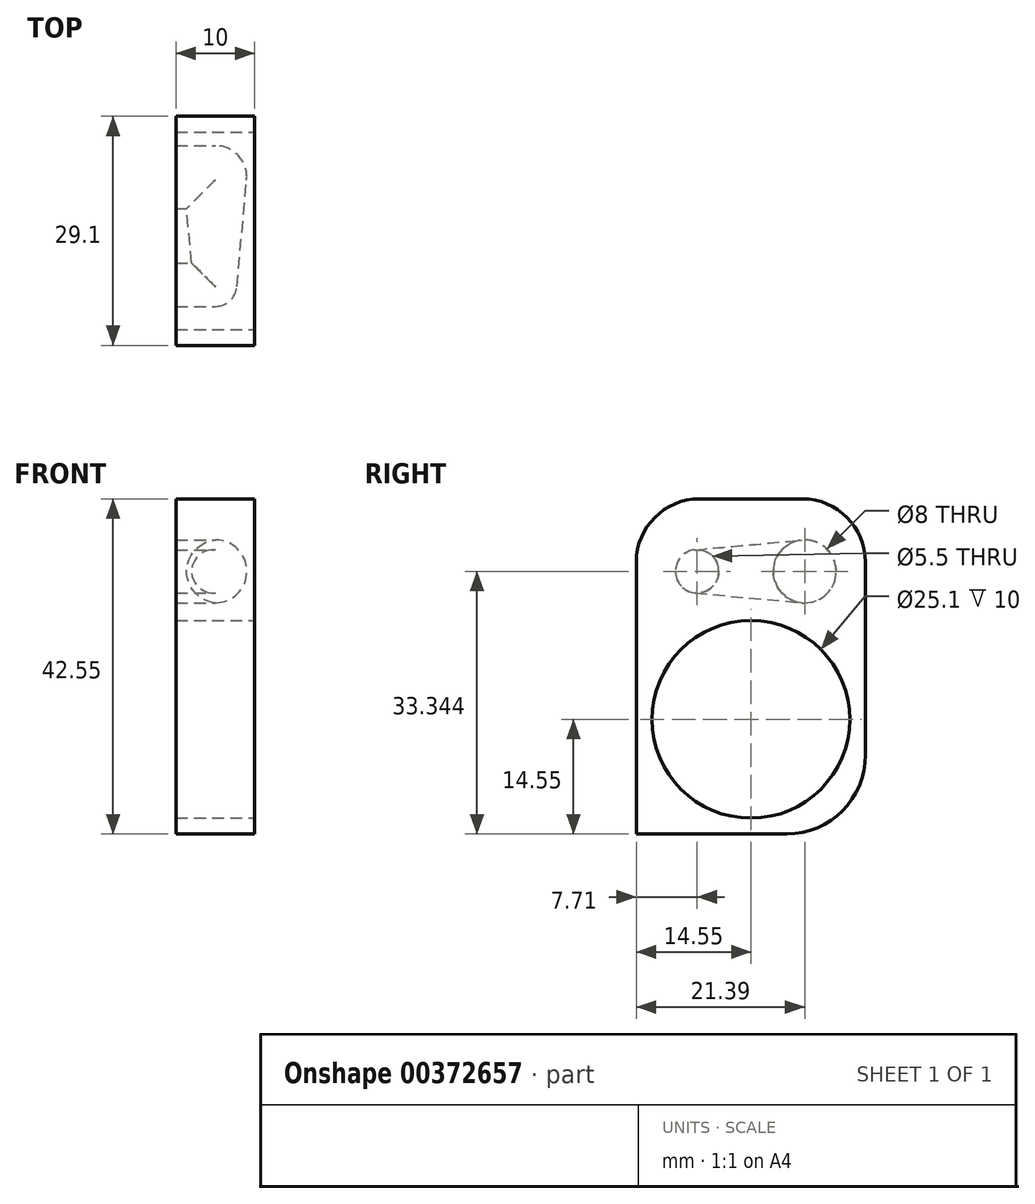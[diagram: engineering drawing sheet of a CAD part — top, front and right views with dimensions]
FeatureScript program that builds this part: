
annotation { "Feature Type Name" : "Feature", "Feature Type Description" : "" }
export const myFeature = defineFeature(function(context is Context, id is Id, definition is map)
    precondition{}
    {
        {
            var Q0;
            Q0=qCreatedBy(makeId("Right.planeOp"),FACE);
            var sketch = newSketch(context, id + "F0", { "sketchPlane" : qUnion([Q0])});
            skCircle(sketch, "E0", {"center": v(0, 0) * mm, "radius": 12.55 * mm});
            skCircle(sketch, "E1", {"center": v(-6.84, 18.8) * mm, "radius": 4.3 * mm, "construction": true});
            skCircle(sketch, "E2", {"center": v(6.84, 18.8) * mm, "radius": 5.1 * mm, "construction": true});
            skLineSegment(sketch, "E3", {"start": v(-6.84, 18.8) * mm, "end": v(0, 0) * mm, "construction": true});
            skLineSegment(sketch, "E4", {"start": v(6.84, 18.8) * mm, "end": v(0, 0) * mm, "construction": true});
            skCircle(sketch, "E5", {"center": v(-27, 0) * mm, "radius": 11 * mm});
            skLineSegment(sketch, "E6", {"start": v(-27, 0) * mm, "end": v(0, 0) * mm, "construction": true});
            skLineSegment(sketch, "E7", {"start": v(6.55, 28) * mm, "end": v(-6.55, 28) * mm});
            skLineSegment(sketch, "E8", {"start": v(14.55, 20) * mm, "end": v(14.55, -14.55) * mm});
            skLineSegment(sketch, "E9", {"start": v(-14.55, 20) * mm, "end": v(-14.55, -14.55) * mm});
            skLineSegment(sketch, "E10", {"start": v(-14.55, -14.55) * mm, "end": v(14.55, -14.55) * mm});
            skCircle(sketch, "E11", {"center": v(-6.84, 18.8) * mm, "radius": 2.75 * mm});
            skCircle(sketch, "E12", {"center": v(6.84, 18.8) * mm, "radius": 4 * mm});
            skLineSegment(sketch, "E13", {"start": v(-9.6, 18.8) * mm, "end": v(10.84, 18.8) * mm});
            skLineSegment(sketch, "E14", {"start": v(-7.1, 21.53) * mm, "end": v(6.84, 22.81) * mm});
            skLineSegment(sketch, "E15", {"start": v(0, 0) * mm, "end": v(0, -14.55) * mm, "construction": true});
            skPoint(sketch, "E16.visualSharp", {"position": v(-14.55, 28) * mm});
            skArc(sketch, "E16.filletArc", {"start": v(-6.55, 28) * mm, "mid": v(-12.2, 25.66) * mm, "end": v(-14.55, 20) * mm});
            skPoint(sketch, "E17.visualSharp", {"position": v(14.55, 28) * mm});
            skArc(sketch, "E17.filletArc", {"start": v(14.55, 20) * mm, "mid": v(12.2, 25.66) * mm, "end": v(6.55, 28) * mm});
            skSolve(sketch);
        }
        {
            var Q0;
            Q0=makeQuery(id+"F0.imprint","IMPRINT",FACE,{"disambiguationData":[TD([[makeQuery(id+"F0.imprint","IMPRINT",EDGE,{"derivedFrom":sQuery(id+"F0.wireOp",EDGE,"E0")}),-1.0]])]});
            var Q1;
            {var subQ0=sQuery(id+"F0.wireOp",EDGE,"E14");var subQ1=sQuery(id+"F0.wireOp",EDGE,"E11");var subQ2=makeQuery(id+"F0.imprint","INTERSECT",VERTEX,{"derivedFrom":[subQ1,subQ0]});Q1=makeQuery(id+"F0.imprint","IMPRINT",FACE,{"disambiguationData":[TD([[makeQuery(id+"F0.imprint","IMPRINT",EDGE,{"disambiguationData":[TD([[subQ2,1.0]])],"derivedFrom":subQ1}),-1.0]])]});}
            extrude(context, id + "F1", {"entities" : qUnion([Q0, Q1]), "oppositeDirection" : true, "depth" : 5 * mm, "offsetDistance" : 25 * mm});
        }
        {
            var Q0;
            Q0=makeQuery(id+"F0.imprint","IMPRINT",FACE,{"disambiguationData":[TD([[makeQuery(id+"F0.imprint","IMPRINT",EDGE,{"derivedFrom":sQuery(id+"F0.wireOp",EDGE,"E0")}),-1.0]])]});
            var Q1;
            {var subQ0=sQuery(id+"F0.wireOp",EDGE,"E13");var subQ1=sQuery(id+"F0.wireOp",EDGE,"E11");var subQ2=makeQuery(id+"F0.imprint","INTERSECT",VERTEX,{"disambiguationData":[OD(0.0)],"derivedFrom":[subQ1,subQ0]});Q1=makeQuery(id+"F0.imprint","IMPRINT",FACE,{"disambiguationData":[TD([[makeQuery(id+"F0.imprint","IMPRINT",EDGE,{"disambiguationData":[TD([[subQ2,-1.0]])],"derivedFrom":subQ1}),1.0]])]});}
            var Q2;
            {var subQ0=sQuery(id+"F0.wireOp",EDGE,"E11");var subQ1=makeQuery(id+"F0.imprint","INTERSECT",VERTEX,{"derivedFrom":[subQ0,sQuery(id+"F0.wireOp",EDGE,"E14")]});Q2=makeQuery(id+"F0.imprint","IMPRINT",FACE,{"disambiguationData":[TD([[makeQuery(id+"F0.imprint","IMPRINT",EDGE,{"disambiguationData":[TD([[subQ1,1.0]])],"derivedFrom":subQ0}),1.0]])]});}
            var Q3;
            {var subQ0=sQuery(id+"F0.wireOp",EDGE,"E14");var subQ1=sQuery(id+"F0.wireOp",EDGE,"E11");var subQ2=makeQuery(id+"F0.imprint","INTERSECT",VERTEX,{"derivedFrom":[subQ1,subQ0]});Q3=makeQuery(id+"F0.imprint","IMPRINT",FACE,{"disambiguationData":[TD([[makeQuery(id+"F0.imprint","IMPRINT",EDGE,{"disambiguationData":[TD([[subQ2,1.0]])],"derivedFrom":subQ1}),-1.0]])]});}
            var Q4;
            {var subQ0=sQuery(id+"F0.wireOp",EDGE,"E13");var subQ1=sQuery(id+"F0.wireOp",EDGE,"E12");var subQ2=makeQuery(id+"F0.imprint","INTERSECT",VERTEX,{"disambiguationData":[OD(0.0)],"derivedFrom":[subQ1,subQ0]});Q4=makeQuery(id+"F0.imprint","IMPRINT",FACE,{"disambiguationData":[TD([[makeQuery(id+"F0.imprint","IMPRINT",EDGE,{"disambiguationData":[TD([[subQ2,-1.0]])],"derivedFrom":subQ1}),1.0]])]});}
            var Q5;
            {var subQ0=sQuery(id+"F0.wireOp",EDGE,"E13");var subQ1=sQuery(id+"F0.wireOp",EDGE,"E12");var subQ2=makeQuery(id+"F0.imprint","INTERSECT",VERTEX,{"disambiguationData":[OD(0.0)],"derivedFrom":[subQ1,subQ0]});Q5=makeQuery(id+"F0.imprint","IMPRINT",FACE,{"disambiguationData":[TD([[makeQuery(id+"F0.imprint","IMPRINT",EDGE,{"disambiguationData":[TD([[subQ2,1.0]])],"derivedFrom":subQ1}),1.0]])]});}
            extrude(context, id + "F2", {"entities" : qUnion([Q0, Q1, Q2, Q3, Q4, Q5]), "operationType" : NewBodyOperationType.ADD, "depth" : 5 * mm, "offsetDistance" : 25 * mm});
        }
        {
            var Q0;
            Q0=makeQuery(id+"F1.opExtrude","SWEPT_EDGE",EDGE,{"disambiguationData":[OSD([sQuery(id+"F0.wireOp",EDGE,"XYx4FfuK-tnTQ-wQDn-o0lU-hYzAaBfXhwYU"),sQuery(id+"F0.wireOp",EDGE,"E7")])]});
            var Q1;
            Q1=makeQuery(id+"F1.opExtrude","SWEPT_EDGE",EDGE,{"disambiguationData":[OSD([sQuery(id+"F0.wireOp",EDGE,"ezvYwHDF-qibp-4aTS-obrj-ytzPbMtdMMT9"),sQuery(id+"F0.wireOp",EDGE,"E8")])]});
            var Q2;
            Q2=makeQuery(id+"F1.opExtrude","SWEPT_EDGE",EDGE,{"disambiguationData":[OSD([sQuery(id+"F0.wireOp",EDGE,"ezvYwHDF-qibp-4aTS-obrj-ytzPbMtdMMT9"),sQuery(id+"F0.wireOp",EDGE,"E7")])]});
            var Q3;
            Q3=makeQuery(id+"F1.opExtrude","SWEPT_EDGE",EDGE,{"disambiguationData":[OSD([sQuery(id+"F0.wireOp",EDGE,"E8"),sQuery(id+"F0.wireOp",EDGE,"E10")])]});
            fillet(context, id + "F3", {"entities" : qUnion([Q0, Q1, Q2, Q3]), "radius" : 10 * mm, "tangentPropagation" : true, "allowEdgeOverflow" : false});
        }
        {
            var Q0;
            {var subQ0=sQuery(id+"F0.wireOp",EDGE,"E11");var subQ1=makeQuery(id+"F0.imprint","INTERSECT",VERTEX,{"derivedFrom":[subQ0,sQuery(id+"F0.wireOp",EDGE,"E14")]});Q0=makeQuery(id+"F0.imprint","IMPRINT",FACE,{"disambiguationData":[TD([[makeQuery(id+"F0.imprint","IMPRINT",EDGE,{"disambiguationData":[TD([[subQ1,1.0]])],"derivedFrom":subQ0}),1.0]])]});}
            var Q1;
            {var subQ0=sQuery(id+"F0.wireOp",EDGE,"E14");var subQ1=sQuery(id+"F0.wireOp",EDGE,"E11");var subQ2=makeQuery(id+"F0.imprint","INTERSECT",VERTEX,{"derivedFrom":[subQ1,subQ0]});Q1=makeQuery(id+"F0.imprint","IMPRINT",FACE,{"disambiguationData":[TD([[makeQuery(id+"F0.imprint","IMPRINT",EDGE,{"disambiguationData":[TD([[subQ2,1.0]])],"derivedFrom":subQ1}),-1.0]])]});}
            var Q2;
            {var subQ0=sQuery(id+"F0.wireOp",EDGE,"E13");var subQ1=sQuery(id+"F0.wireOp",EDGE,"E12");var subQ2=makeQuery(id+"F0.imprint","INTERSECT",VERTEX,{"disambiguationData":[OD(0.0)],"derivedFrom":[subQ1,subQ0]});Q2=makeQuery(id+"F0.imprint","IMPRINT",FACE,{"disambiguationData":[TD([[makeQuery(id+"F0.imprint","IMPRINT",EDGE,{"disambiguationData":[TD([[subQ2,-1.0]])],"derivedFrom":subQ1}),1.0]])]});}
            var Q3;
            Q3=sQuery(id+"F0.wireOp",EDGE,"E13");
            revolve(context, id + "F4", {"operationType" : NewBodyOperationType.REMOVE, "surfaceOperationType" : NewSurfaceOperationType.NEW, "entities" : qUnion([Q0, Q1, Q2]), "axis" : qUnion([Q3]), "revolveType" : RevolveType.FULL, "oppositeDirection" : true});
        }
    });
